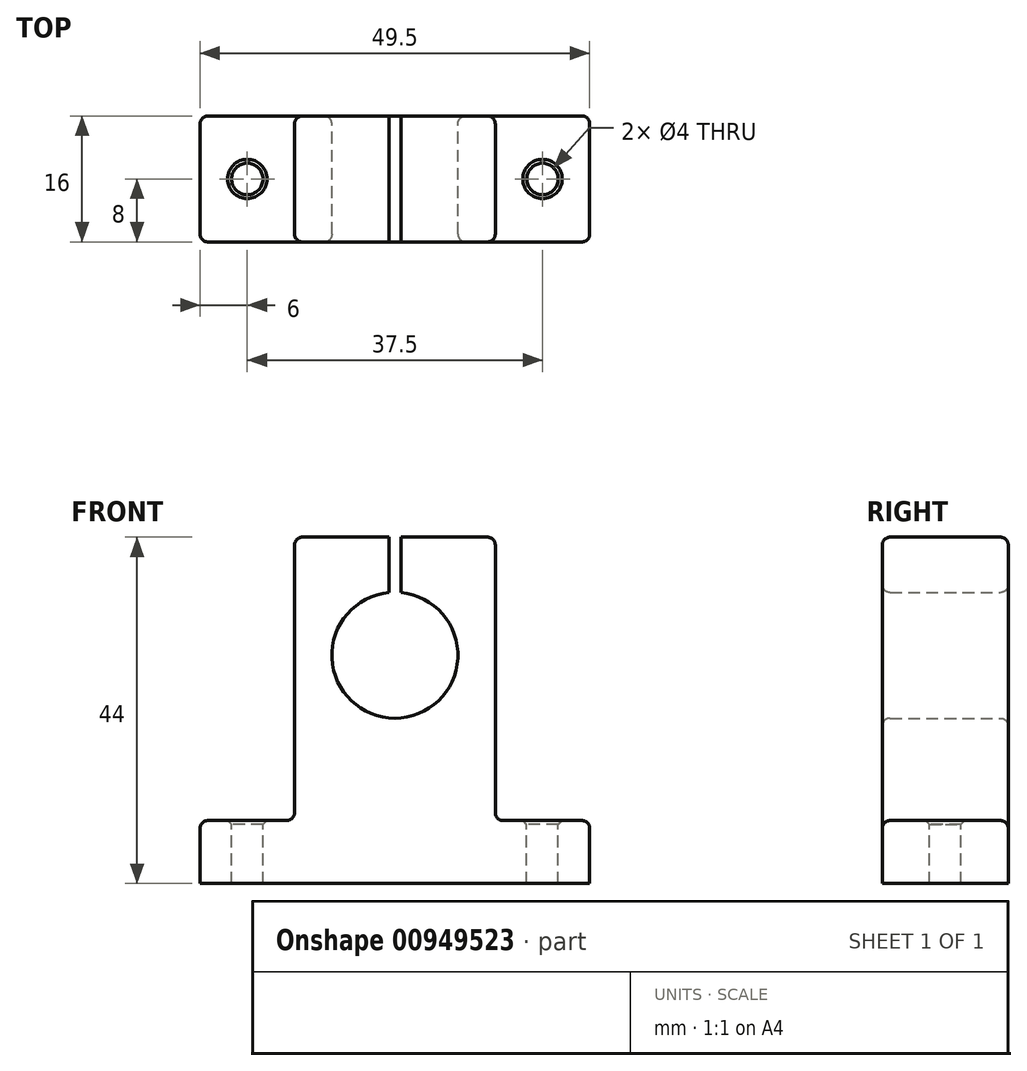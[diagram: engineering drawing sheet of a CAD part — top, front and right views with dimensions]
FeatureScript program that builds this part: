
annotation { "Feature Type Name" : "Feature", "Feature Type Description" : "" }
export const myFeature = defineFeature(function(context is Context, id is Id, definition is map)
    precondition{}
    {
        {
            var Q0;
            Q0=qCreatedBy(makeId("Front.planeOp"),FACE);
            var sketch = newSketch(context, id + "F0", { "sketchPlane" : qUnion([Q0])});
            skLineSegment(sketch, "E0", {"start": v(0, -11.64) * mm, "end": v(0, 43.14) * mm, "construction": true});
            skLineSegment(sketch, "E1", {"start": v(24.75, -5.64) * mm, "end": v(-24.75, -5.64) * mm});
            skLineSegment(sketch, "E2", {"start": v(-24.75, -5.64) * mm, "end": v(-24.75, 2.36) * mm});
            skLineSegment(sketch, "E3", {"start": v(-24.75, 2.36) * mm, "end": v(-12.75, 2.36) * mm});
            skLineSegment(sketch, "E4", {"start": v(-12.75, 2.36) * mm, "end": v(-12.75, 38.36) * mm});
            skLineSegment(sketch, "E5", {"start": v(-12.75, 38.36) * mm, "end": v(-0.75, 38.36) * mm});
            skLineSegment(sketch, "E6", {"start": v(12.75, 38.36) * mm, "end": v(12.75, 2.36) * mm});
            skLineSegment(sketch, "E7", {"start": v(12.75, 2.36) * mm, "end": v(24.75, 2.36) * mm});
            skLineSegment(sketch, "E8", {"start": v(24.75, 2.36) * mm, "end": v(24.75, -5.64) * mm});
            skArc(sketch, "E9", {"start": v(-0.75, 31.33) * mm, "mid": v(0, 15.36) * mm, "end": v(0.75, 31.33) * mm});
            skLineSegment(sketch, "E10", {"start": v(-0.75, 38.36) * mm, "end": v(-0.75, 31.33) * mm});
            skLineSegment(sketch, "E11", {"start": v(0.75, 38.36) * mm, "end": v(0.75, 31.33) * mm});
            skLineSegment(sketch, "E12.trimOffspring", {"start": v(0.75, 38.36) * mm, "end": v(12.75, 38.36) * mm});
            skSolve(sketch);
        }
        {
            var Q0;
            Q0 = qSketchRegion(id + "F0", true);
            extrude(context, id + "F1", {"entities" : qUnion([Q0]), "endBound" : BoundingType.SYMMETRIC, "depth" : 16 * mm, "offsetDistance" : 25 * mm});
        }
        {
            var Q0;
            Q0=makeQuery(id+"F1.opExtrude","SWEPT_FACE",FACE,{"disambiguationData":[OSD([sQuery(id+"F0.wireOp",EDGE,"E7")])]});
            var sketch = newSketch(context, id + "F2", { "sketchPlane" : qUnion([Q0])});
            skPoint(sketch, "E13", {"position": v(18.75, 0) * mm});
            skPoint(sketch, "E13.positionSnap0", {"position": v(18.75, 8) * mm});
            skLineSegment(sketch, "E14", {"start": v(0, 10.11) * mm, "end": v(0, -9.34) * mm, "construction": true});
            skPoint(sketch, "E15.MirrorP", {"position": v(-18.75, 0) * mm});
            skSolve(sketch);
        }
        {
            var Q0;
            Q0=sQuery(id+"F2.wireOp",VERTEX,"E13");
            var Q1;
            Q1=sQuery(id+"F2.wireOp",VERTEX,"E15.MirrorP");
            var Q2;
            Q2=makeQuery(id+"F1.opExtrude","SWEPT_BODY",BODY,{"disambiguationData":[OSD([sQuery(id+"F0.wireOp",EDGE,"E1"),sQuery(id+"F0.wireOp",EDGE,"E2"),sQuery(id+"F0.wireOp",EDGE,"E3"),sQuery(id+"F0.wireOp",EDGE,"E4"),sQuery(id+"F0.wireOp",EDGE,"E5"),sQuery(id+"F0.wireOp",EDGE,"E6"),sQuery(id+"F0.wireOp",EDGE,"E7"),sQuery(id+"F0.wireOp",EDGE,"E8"),sQuery(id+"F0.wireOp",EDGE,"E9"),sQuery(id+"F0.wireOp",EDGE,"E10"),sQuery(id+"F0.wireOp",EDGE,"E11"),sQuery(id+"F0.wireOp",EDGE,"E12.trimOffspring")])]});
            hole(context, id + "F3", {"style" : HoleStyle.C_SINK, "endStyle" : HoleEndStyle.THROUGH, "holeDiameter" : 4 * mm, "cSinkDiameter" : 5 * mm, "cSinkAngle" : 90 * degree, "majorDiameter" : 5 * mm, "isTappedThrough" : true, "tappedDepth" : 12 * mm, "tapClearance" : 3, "locations" : qUnion([Q0, Q1]), "scope" : qUnion([Q2])});
        }
        {
            var Q0;
            Q0=makeQuery(id+"F1.opExtrude","CAP_EDGE",EDGE,{"disambiguationData":[OSD([sQuery(id+"F0.wireOp",EDGE,"E4")])],"isStart":false});
            var Q1;
            Q1=makeQuery(id+"F1.opExtrude","CAP_EDGE",EDGE,{"disambiguationData":[OSD([sQuery(id+"F0.wireOp",EDGE,"E3")])],"isStart":false});
            var Q2;
            Q2=makeQuery(id+"F1.opExtrude","CAP_EDGE",EDGE,{"disambiguationData":[OSD([sQuery(id+"F0.wireOp",EDGE,"E2")])],"isStart":false});
            var Q3;
            Q3=makeQuery(id+"F1.opExtrude","CAP_EDGE",EDGE,{"disambiguationData":[OSD([sQuery(id+"F0.wireOp",EDGE,"E5")])],"isStart":false});
            var Q4;
            Q4=makeQuery(id+"F1.opExtrude","CAP_EDGE",EDGE,{"disambiguationData":[OSD([sQuery(id+"F0.wireOp",EDGE,"E12.trimOffspring")])],"isStart":false});
            var Q5;
            Q5=makeQuery(id+"F1.opExtrude","CAP_EDGE",EDGE,{"disambiguationData":[OSD([sQuery(id+"F0.wireOp",EDGE,"E6")])],"isStart":false});
            var Q6;
            Q6=makeQuery(id+"F1.opExtrude","CAP_EDGE",EDGE,{"disambiguationData":[OSD([sQuery(id+"F0.wireOp",EDGE,"E7")])],"isStart":false});
            var Q7;
            Q7=makeQuery(id+"F1.opExtrude","CAP_EDGE",EDGE,{"disambiguationData":[OSD([sQuery(id+"F0.wireOp",EDGE,"E8")])],"isStart":false});
            var Q8;
            Q8=makeQuery(id+"F1.opExtrude","CAP_EDGE",EDGE,{"disambiguationData":[OSD([sQuery(id+"F0.wireOp",EDGE,"E9")])],"isStart":false});
            var Q9;
            Q9=makeQuery(id+"F1.opExtrude","CAP_EDGE",EDGE,{"disambiguationData":[OSD([sQuery(id+"F0.wireOp",EDGE,"E8")])],"isStart":true});
            var Q10;
            Q10=makeQuery(id+"F1.opExtrude","CAP_EDGE",EDGE,{"disambiguationData":[OSD([sQuery(id+"F0.wireOp",EDGE,"E7")])],"isStart":true});
            var Q11;
            Q11=makeQuery(id+"F1.opExtrude","CAP_EDGE",EDGE,{"disambiguationData":[OSD([sQuery(id+"F0.wireOp",EDGE,"E6")])],"isStart":true});
            var Q12;
            Q12=makeQuery(id+"F1.opExtrude","CAP_EDGE",EDGE,{"disambiguationData":[OSD([sQuery(id+"F0.wireOp",EDGE,"E12.trimOffspring")])],"isStart":true});
            var Q13;
            Q13=makeQuery(id+"F1.opExtrude","CAP_EDGE",EDGE,{"disambiguationData":[OSD([sQuery(id+"F0.wireOp",EDGE,"E5")])],"isStart":true});
            var Q14;
            Q14=makeQuery(id+"F1.opExtrude","CAP_EDGE",EDGE,{"disambiguationData":[OSD([sQuery(id+"F0.wireOp",EDGE,"E4")])],"isStart":true});
            var Q15;
            Q15=makeQuery(id+"F1.opExtrude","CAP_EDGE",EDGE,{"disambiguationData":[OSD([sQuery(id+"F0.wireOp",EDGE,"E3")])],"isStart":true});
            var Q16;
            Q16=makeQuery(id+"F1.opExtrude","CAP_EDGE",EDGE,{"disambiguationData":[OSD([sQuery(id+"F0.wireOp",EDGE,"E2")])],"isStart":true});
            var Q17;
            Q17=makeQuery(id+"F1.opExtrude","CAP_EDGE",EDGE,{"disambiguationData":[OSD([sQuery(id+"F0.wireOp",EDGE,"E9")])],"isStart":true});
            var Q18;
            Q18=makeQuery(id+"F1.opExtrude","SWEPT_EDGE",EDGE,{"disambiguationData":[OSD([sQuery(id+"F0.wireOp",EDGE,"E6"),sQuery(id+"F0.wireOp",EDGE,"E7")])]});
            var Q19;
            Q19=makeQuery(id+"F1.opExtrude","SWEPT_EDGE",EDGE,{"disambiguationData":[OSD([sQuery(id+"F0.wireOp",EDGE,"E7"),sQuery(id+"F0.wireOp",EDGE,"E8")])]});
            var Q20;
            Q20=makeQuery(id+"F1.opExtrude","SWEPT_EDGE",EDGE,{"disambiguationData":[OSD([sQuery(id+"F0.wireOp",EDGE,"E6"),sQuery(id+"F0.wireOp",EDGE,"E12.trimOffspring")])]});
            var Q21;
            Q21=makeQuery(id+"F1.opExtrude","SWEPT_EDGE",EDGE,{"disambiguationData":[OSD([sQuery(id+"F0.wireOp",EDGE,"E2"),sQuery(id+"F0.wireOp",EDGE,"E3")])]});
            var Q22;
            Q22=makeQuery(id+"F1.opExtrude","SWEPT_EDGE",EDGE,{"disambiguationData":[OSD([sQuery(id+"F0.wireOp",EDGE,"E3"),sQuery(id+"F0.wireOp",EDGE,"E4")])]});
            var Q23;
            Q23=makeQuery(id+"F1.opExtrude","SWEPT_EDGE",EDGE,{"disambiguationData":[OSD([sQuery(id+"F0.wireOp",EDGE,"E4"),sQuery(id+"F0.wireOp",EDGE,"E5")])]});
            fillet(context, id + "F4", {"entities" : qUnion([Q0, Q1, Q2, Q3, Q4, Q5, Q6, Q7, Q8, Q9, Q10, Q11, Q12, Q13, Q14, Q15, Q16, Q17, Q18, Q19, Q20, Q21, Q22, Q23]), "radius" : 1 * mm, "tangentPropagation" : true, "allowEdgeOverflow" : false});
        }
    });
